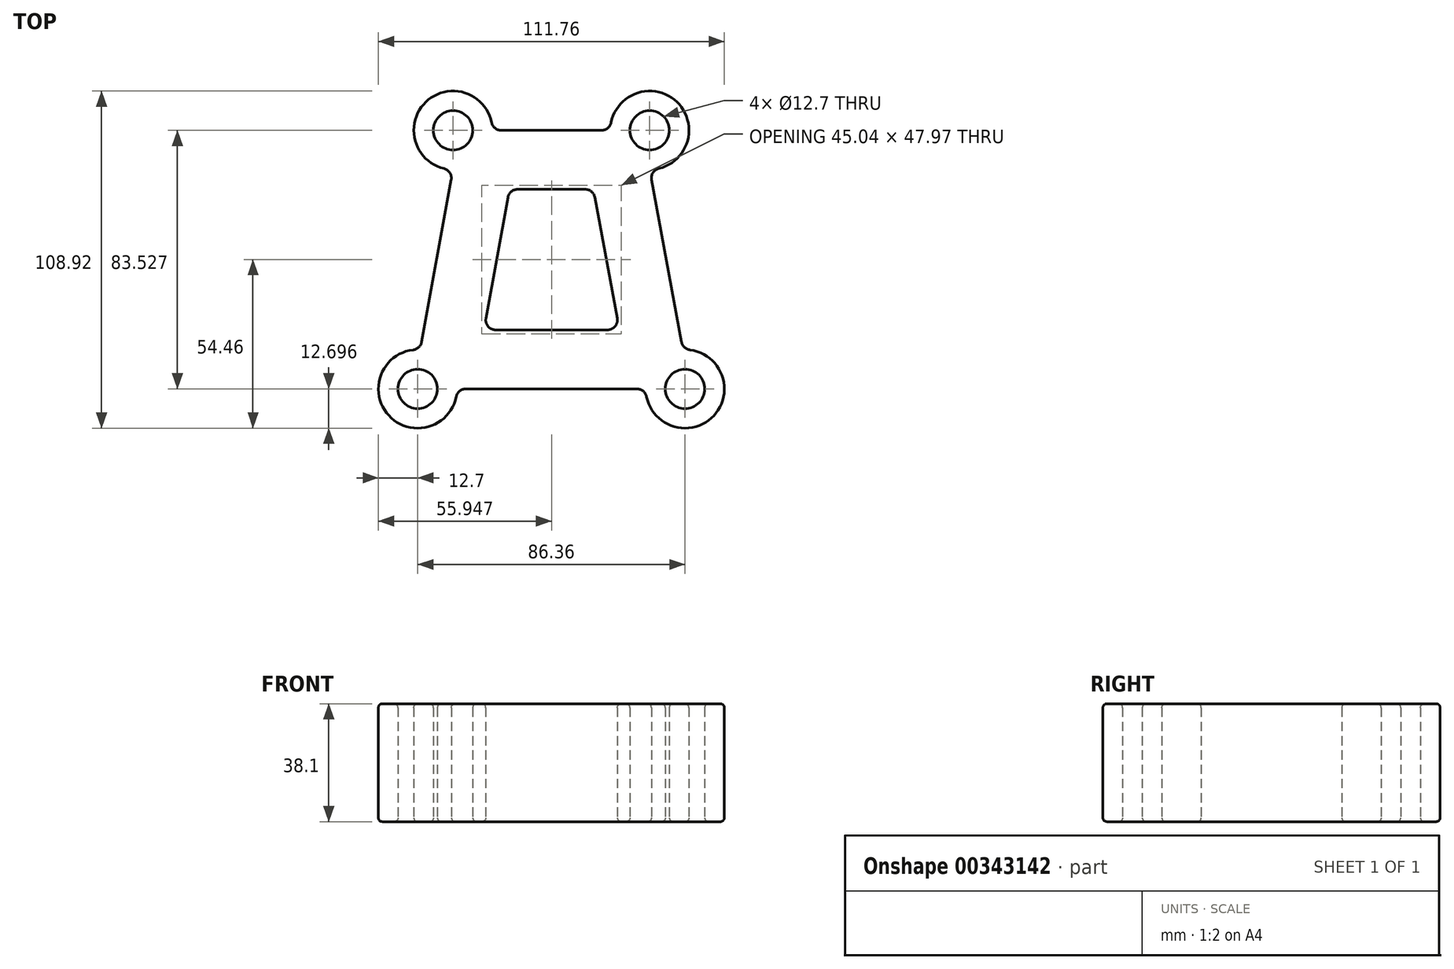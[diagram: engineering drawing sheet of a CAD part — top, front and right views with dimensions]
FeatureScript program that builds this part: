
annotation { "Feature Type Name" : "Feature", "Feature Type Description" : "" }
export const myFeature = defineFeature(function(context is Context, id is Id, definition is map)
    precondition{}
    {
        {
            var Q0;
            Q0=qCreatedBy(makeId("Top.planeOp"),FACE);
            var sketch = newSketch(context, id + "F0", { "sketchPlane" : qUnion([Q0])});
            skLineSegment(sketch, "E0.bottom", {"start": v(31.75, 41.76) * mm, "end": v(-31.75, 41.76) * mm, "construction": true});
            skLineSegment(sketch, "E0.top", {"start": v(31.75, -41.76) * mm, "end": v(-31.75, -41.76) * mm, "construction": true});
            skLineSegment(sketch, "E0.left", {"start": v(31.75, 41.76) * mm, "end": v(31.75, -41.76) * mm, "construction": true});
            skLineSegment(sketch, "E0.right", {"start": v(-31.75, 41.76) * mm, "end": v(-31.75, 29.06) * mm, "construction": true});
            skPoint(sketch, "E0.middle", {"position": v(0, 0) * mm});
            skCircle(sketch, "E1", {"center": v(31.75, 41.76) * mm, "radius": 6.35 * mm});
            skCircle(sketch, "E2", {"center": v(-31.75, 41.76) * mm, "radius": 6.35 * mm});
            skCircle(sketch, "E3", {"center": v(-43.18, -41.76) * mm, "radius": 6.35 * mm});
            skCircle(sketch, "E4", {"center": v(43.18, -41.76) * mm, "radius": 6.35 * mm});
            skLineSegment(sketch, "E5", {"start": v(43.18, -41.76) * mm, "end": v(31.75, -41.76) * mm, "construction": true});
            skLineSegment(sketch, "E6", {"start": v(-31.75, -41.76) * mm, "end": v(-43.18, -41.76) * mm, "construction": true});
            skArc(sketch, "E7.0", {"start": v(-19.3, 44.3) * mm, "mid": v(-40.57, 50.9) * mm, "end": v(-34.73, 29.42) * mm});
            skArc(sketch, "E8.0", {"start": v(-44.64, -29.15) * mm, "mid": v(-52.54, -50.35) * mm, "end": v(-30.74, -44.3) * mm});
            skArc(sketch, "E9.0", {"start": v(34.74, 29.42) * mm, "mid": v(40.57, 50.9) * mm, "end": v(19.3, 44.3) * mm});
            skArc(sketch, "E10.0", {"start": v(30.74, -44.3) * mm, "mid": v(52.5, -50.4) * mm, "end": v(44.78, -29.16) * mm});
            skLineSegment(sketch, "E11", {"start": v(-31.75, 29.06) * mm, "end": v(-31.75, -23.13) * mm, "construction": true});
            skLineSegment(sketch, "E12", {"start": v(-27.63, -41.76) * mm, "end": v(27.63, -41.76) * mm});
            skLineSegment(sketch, "E13", {"start": v(42.05, -26.6) * mm, "end": v(32.36, 25.76) * mm});
            skLineSegment(sketch, "E14", {"start": v(16.2, 41.76) * mm, "end": v(-16.2, 41.76) * mm});
            skLineSegment(sketch, "E15", {"start": v(-41.88, -26.56) * mm, "end": v(-32.35, 25.76) * mm});
            skLineSegment(sketch, "E16.trimOffspring", {"start": v(-31.75, -23.13) * mm, "end": v(-31.75, -41.76) * mm, "construction": true});
            skLineSegment(sketch, "E17.0", {"start": v(-21.14, -18.97) * mm, "end": v(-14.02, 20.1) * mm});
            skLineSegment(sketch, "E18.0", {"start": v(21.27, -18.96) * mm, "end": v(14.03, 20.12) * mm});
            skLineSegment(sketch, "E19.0", {"start": v(18.15, -22.71) * mm, "end": v(-18.01, -22.71) * mm});
            skLineSegment(sketch, "E20.0", {"start": v(10.91, 22.71) * mm, "end": v(-10.9, 22.71) * mm});
            skPoint(sketch, "E21.visualSharp", {"position": v(-13.54, 22.71) * mm});
            skArc(sketch, "E21.filletArc", {"start": v(-10.9, 22.71) * mm, "mid": v(-12.93, 21.98) * mm, "end": v(-14.02, 20.1) * mm});
            skPoint(sketch, "E22.visualSharp", {"position": v(13.55, 22.71) * mm});
            skArc(sketch, "E22.filletArc", {"start": v(14.03, 20.12) * mm, "mid": v(12.94, 21.98) * mm, "end": v(10.91, 22.71) * mm});
            skPoint(sketch, "E23.visualSharp", {"position": v(21.96, -22.71) * mm});
            skArc(sketch, "E23.filletArc", {"start": v(18.15, -22.71) * mm, "mid": v(20.59, -21.57) * mm, "end": v(21.27, -18.96) * mm});
            skPoint(sketch, "E24.visualSharp", {"position": v(-21.82, -22.71) * mm});
            skArc(sketch, "E24.filletArc", {"start": v(-21.14, -18.97) * mm, "mid": v(-20.45, -21.57) * mm, "end": v(-18.01, -22.71) * mm});
            skPoint(sketch, "E25.visualSharp", {"position": v(-31.75, 29.06) * mm});
            skArc(sketch, "E25.filletArc", {"start": v(-32.35, 25.76) * mm, "mid": v(-32.81, 28.06) * mm, "end": v(-34.73, 29.42) * mm});
            skPoint(sketch, "E26.visualSharp", {"position": v(-19.05, 41.76) * mm});
            skArc(sketch, "E26.filletArc", {"start": v(-19.3, 44.3) * mm, "mid": v(-18.2, 42.48) * mm, "end": v(-16.2, 41.76) * mm});
            skPoint(sketch, "E27.visualSharp", {"position": v(19.05, 41.76) * mm});
            skArc(sketch, "E27.filletArc", {"start": v(16.2, 41.76) * mm, "mid": v(18.2, 42.48) * mm, "end": v(19.3, 44.3) * mm});
            skPoint(sketch, "E28.visualSharp", {"position": v(31.75, 29.06) * mm});
            skArc(sketch, "E28.filletArc", {"start": v(34.74, 29.42) * mm, "mid": v(32.82, 28.06) * mm, "end": v(32.36, 25.76) * mm});
            skPoint(sketch, "E29.visualSharp", {"position": v(42.52, -29.08) * mm});
            skArc(sketch, "E29.filletArc", {"start": v(42.05, -26.6) * mm, "mid": v(43, -28.32) * mm, "end": v(44.78, -29.16) * mm});
            skPoint(sketch, "E30.visualSharp", {"position": v(30.48, -41.76) * mm});
            skArc(sketch, "E30.filletArc", {"start": v(30.74, -44.3) * mm, "mid": v(29.63, -42.48) * mm, "end": v(27.63, -41.76) * mm});
            skPoint(sketch, "E31.visualSharp", {"position": v(-30.48, -41.76) * mm});
            skArc(sketch, "E31.filletArc", {"start": v(-27.63, -41.76) * mm, "mid": v(-29.63, -42.48) * mm, "end": v(-30.74, -44.3) * mm});
            skPoint(sketch, "E32.visualSharp", {"position": v(-42.34, -29.1) * mm});
            skArc(sketch, "E32.filletArc", {"start": v(-44.64, -29.15) * mm, "mid": v(-42.83, -28.31) * mm, "end": v(-41.88, -26.56) * mm});
            skSolve(sketch);
        }
        {
            var Q0;
            Q0 = qSketchRegion(id + "F0", true);
            extrude(context, id + "F1", {"entities" : qUnion([Q0]), "depth" : 38.1 * mm});
        }
        {
            var Q0;
            Q0=makeQuery(id+"F1.opExtrude","CAP_FACE",FACE,{"disambiguationData":[OSD([sQuery(id+"F0.wireOp",EDGE,"E1"),sQuery(id+"F0.wireOp",EDGE,"E2"),sQuery(id+"F0.wireOp",EDGE,"E3"),sQuery(id+"F0.wireOp",EDGE,"E4"),sQuery(id+"F0.wireOp",EDGE,"E7.0"),sQuery(id+"F0.wireOp",EDGE,"E8.0"),sQuery(id+"F0.wireOp",EDGE,"E9.0"),sQuery(id+"F0.wireOp",EDGE,"E10.0"),sQuery(id+"F0.wireOp",EDGE,"E12"),sQuery(id+"F0.wireOp",EDGE,"E13"),sQuery(id+"F0.wireOp",EDGE,"E14"),sQuery(id+"F0.wireOp",EDGE,"E15"),sQuery(id+"F0.wireOp",EDGE,"E17.0"),sQuery(id+"F0.wireOp",EDGE,"E18.0"),sQuery(id+"F0.wireOp",EDGE,"E19.0"),sQuery(id+"F0.wireOp",EDGE,"E20.0"),sQuery(id+"F0.wireOp",EDGE,"E21.filletArc"),sQuery(id+"F0.wireOp",EDGE,"E22.filletArc"),sQuery(id+"F0.wireOp",EDGE,"E23.filletArc"),sQuery(id+"F0.wireOp",EDGE,"E24.filletArc"),sQuery(id+"F0.wireOp",EDGE,"E25.filletArc"),sQuery(id+"F0.wireOp",EDGE,"E26.filletArc"),sQuery(id+"F0.wireOp",EDGE,"E27.filletArc"),sQuery(id+"F0.wireOp",EDGE,"E28.filletArc"),sQuery(id+"F0.wireOp",EDGE,"E29.filletArc"),sQuery(id+"F0.wireOp",EDGE,"E30.filletArc"),sQuery(id+"F0.wireOp",EDGE,"E31.filletArc"),sQuery(id+"F0.wireOp",EDGE,"E32.filletArc")])],"isStart":false});
            var Q1;
            Q1=makeQuery(id+"F1.opExtrude","CAP_FACE",FACE,{"disambiguationData":[OSD([sQuery(id+"F0.wireOp",EDGE,"E1"),sQuery(id+"F0.wireOp",EDGE,"E2"),sQuery(id+"F0.wireOp",EDGE,"E3"),sQuery(id+"F0.wireOp",EDGE,"E4"),sQuery(id+"F0.wireOp",EDGE,"E7.0"),sQuery(id+"F0.wireOp",EDGE,"E8.0"),sQuery(id+"F0.wireOp",EDGE,"E9.0"),sQuery(id+"F0.wireOp",EDGE,"E10.0"),sQuery(id+"F0.wireOp",EDGE,"E12"),sQuery(id+"F0.wireOp",EDGE,"E13"),sQuery(id+"F0.wireOp",EDGE,"E14"),sQuery(id+"F0.wireOp",EDGE,"E15"),sQuery(id+"F0.wireOp",EDGE,"E17.0"),sQuery(id+"F0.wireOp",EDGE,"E18.0"),sQuery(id+"F0.wireOp",EDGE,"E19.0"),sQuery(id+"F0.wireOp",EDGE,"E20.0"),sQuery(id+"F0.wireOp",EDGE,"E21.filletArc"),sQuery(id+"F0.wireOp",EDGE,"E22.filletArc"),sQuery(id+"F0.wireOp",EDGE,"E23.filletArc"),sQuery(id+"F0.wireOp",EDGE,"E24.filletArc"),sQuery(id+"F0.wireOp",EDGE,"E25.filletArc"),sQuery(id+"F0.wireOp",EDGE,"E26.filletArc"),sQuery(id+"F0.wireOp",EDGE,"E27.filletArc"),sQuery(id+"F0.wireOp",EDGE,"E28.filletArc"),sQuery(id+"F0.wireOp",EDGE,"E29.filletArc"),sQuery(id+"F0.wireOp",EDGE,"E30.filletArc"),sQuery(id+"F0.wireOp",EDGE,"E31.filletArc"),sQuery(id+"F0.wireOp",EDGE,"E32.filletArc")])],"isStart":true});
            fillet(context, id + "F2", {"entities" : qUnion([Q0, Q1]), "radius" : 1.27 * mm, "tangentPropagation" : true, "allowEdgeOverflow" : false});
        }
    });
